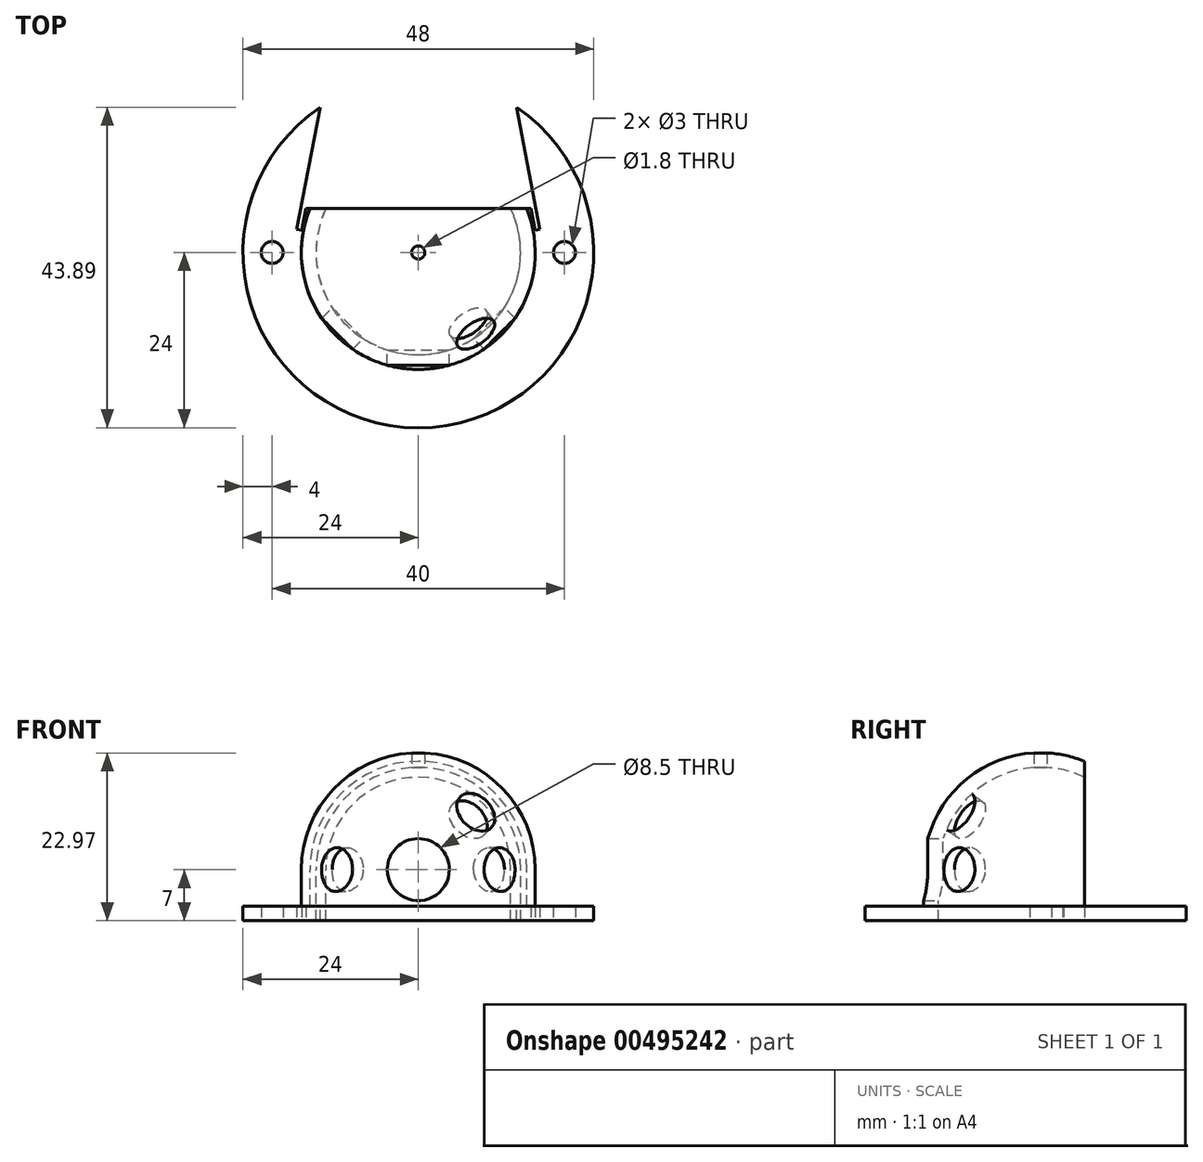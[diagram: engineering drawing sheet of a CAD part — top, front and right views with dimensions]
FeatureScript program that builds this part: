
annotation { "Feature Type Name" : "Feature", "Feature Type Description" : "" }
export const myFeature = defineFeature(function(context is Context, id is Id, definition is map)
    precondition{}
    {
        {
            var Q0;
            Q0=qCreatedBy(makeId("Front.planeOp"),FACE);
            var sketch = newSketch(context, id + "F0", { "sketchPlane" : qUnion([Q0])});
            skLineSegment(sketch, "E0", {"start": v(-14, -7) * mm, "end": v(-24, -7) * mm});
            skLineSegment(sketch, "E1", {"start": v(-24, -7) * mm, "end": v(-24, -5) * mm});
            skLineSegment(sketch, "E2", {"start": v(-24, -5) * mm, "end": v(-16, -5) * mm});
            skLineSegment(sketch, "E3", {"start": v(-16, -5) * mm, "end": v(-16, 0) * mm});
            skLineSegment(sketch, "E4", {"start": v(-14, -7) * mm, "end": v(-14, 0) * mm});
            skArc(sketch, "E5", {"start": v(0, 14) * mm, "mid": v(-9.9, 9.9) * mm, "end": v(-14, 0) * mm});
            skArc(sketch, "E6", {"start": v(0, 16) * mm, "mid": v(-11.31, 11.31) * mm, "end": v(-16, 0) * mm});
            skLineSegment(sketch, "E7", {"start": v(0, 16) * mm, "end": v(0, 14) * mm});
            skSolve(sketch);
        }
        {
            var Q0;
            Q0=qSketchRegion(id+"F0",true);
            var Q1;
            Q1=sQuery(id+"F0.wireOp",EDGE,"E7");
            revolve(context, id + "F1", {"entities" : qUnion([Q0]), "axis" : qUnion([Q1]), "revolveType" : RevolveType.FULL});
        }
        {
            var Q0;
            Q0=qCreatedBy(makeId("Front.planeOp"),FACE);
            var sketch = newSketch(context, id + "F2", { "sketchPlane" : qUnion([Q0])});
            skCircle(sketch, "E8", {"center": v(0, 0) * mm, "radius": 4.25 * mm});
            skSolve(sketch);
        }
        {
            var Q0;
            Q0=qSketchRegion(id+"F2",true);
            extrude(context, id + "F3", {"entities" : qUnion([Q0]), "operationType" : NewBodyOperationType.REMOVE, "depth" : 50 * mm});
        }
        {
            var Q0;
            Q0=qCreatedBy(makeId("Top.planeOp"),FACE);
            var sketch = newSketch(context, id + "F4", { "sketchPlane" : qUnion([Q0])});
            skLineSegment(sketch, "E9", {"start": v(-39.11, -39.11) * mm, "end": v(32.62, 32.62) * mm, "construction": true});
            skLineSegment(sketch, "E10", {"start": v(-37.35, 37.35) * mm, "end": v(42.98, -42.98) * mm, "construction": true});
            skSolve(sketch);
        }
        {
            var Q0;
            Q0=sQuery(id+"F4.wireOp",EDGE,"E10");
            cPlane(context, id + "F5", {"entities" : qUnion([Q0]), "cplaneType" : CPlaneType.LINE_ANGLE, "offset" : 25 * mm, "angle" : 90 * degree, "width" : 150 * mm, "height" : 150 * mm});
        }
        {
            var Q0;
            Q0=qCreatedBy(id+"F5.planeOp",FACE);
            var sketch = newSketch(context, id + "F6", { "sketchPlane" : qUnion([Q0])});
            skCircle(sketch, "E11", {"center": v(0, 0) * mm, "radius": 3 * mm});
            skSolve(sketch);
        }
        {
            var Q0;
            Q0=qSketchRegion(id+"F6",true);
            extrude(context, id + "F7", {"entities" : qUnion([Q0]), "operationType" : NewBodyOperationType.REMOVE, "oppositeDirection" : true, "depth" : 25 * mm});
        }
        {
            var Q0;
            Q0=qCreatedBy(makeId("Front.planeOp"),FACE);
            var sketch = newSketch(context, id + "F8", { "sketchPlane" : qUnion([Q0])});
            skLineSegment(sketch, "E12", {"start": v(0, 0) * mm, "end": v(30.29, 30.29) * mm, "construction": true});
            skLineSegment(sketch, "E13", {"start": v(0, 0) * mm, "end": v(-31.13, 31.13) * mm, "construction": true});
            skSolve(sketch);
        }
        {
            var Q0;
            Q0=sQuery(id+"F8.wireOp",EDGE,"E12");
            cPlane(context, id + "F9", {"entities" : qUnion([Q0]), "cplaneType" : CPlaneType.LINE_ANGLE, "offset" : 25 * mm, "angle" : 90 * degree, "width" : 150 * mm, "height" : 150 * mm});
        }
        {
            var Q0;
            Q0=qCreatedBy(id+"F9.planeOp",FACE);
            var sketch = newSketch(context, id + "F10", { "sketchPlane" : qUnion([Q0])});
            skLineSegment(sketch, "E14", {"start": v(0, 0) * mm, "end": v(19.81, 19.81) * mm, "construction": true});
            skLineSegment(sketch, "E15", {"start": v(16.68, 16.68) * mm, "end": v(14.56, 18.8) * mm});
            skLineSegment(sketch, "E16", {"start": v(14.56, 18.8) * mm, "end": v(1.88, 6.12) * mm});
            skLineSegment(sketch, "E17", {"start": v(1.88, 6.12) * mm, "end": v(4, 4) * mm});
            skLineSegment(sketch, "E18", {"start": v(4, 4) * mm, "end": v(16.68, 16.68) * mm});
            skSolve(sketch);
        }
        {
            var Q0;
            Q0=qSketchRegion(id+"F10",true);
            var Q1;
            Q1=sQuery(id+"F10.wireOp",EDGE,"E18");
            revolve(context, id + "F11", {"operationType" : NewBodyOperationType.REMOVE, "entities" : qUnion([Q0]), "axis" : qUnion([Q1]), "revolveType" : RevolveType.FULL, "oppositeDirection" : true});
        }
        {
            var Q0;
            Q0=sQuery(id+"F4.wireOp",EDGE,"E9");
            cPlane(context, id + "F12", {"entities" : qUnion([Q0]), "cplaneType" : CPlaneType.LINE_ANGLE, "offset" : 25 * mm, "angle" : 90 * degree, "width" : 150 * mm, "height" : 150 * mm});
        }
        {
            var Q0;
            Q0=qCreatedBy(id+"F12.planeOp",FACE);
            var sketch = newSketch(context, id + "F13", { "sketchPlane" : qUnion([Q0])});
            skCircle(sketch, "E19", {"center": v(0, 0) * mm, "radius": 3 * mm});
            skSolve(sketch);
        }
        {
            var Q0;
            Q0=qSketchRegion(id+"F13",true);
            extrude(context, id + "F14", {"entities" : qUnion([Q0]), "operationType" : NewBodyOperationType.REMOVE, "depth" : 25 * mm});
        }
        {
            var Q0;
            Q0=sQuery(id+"F8.wireOp",EDGE,"E13");
            cPlane(context, id + "F15", {"entities" : qUnion([Q0]), "cplaneType" : CPlaneType.LINE_ANGLE, "offset" : 25 * mm, "angle" : 90 * degree, "width" : 150 * mm, "height" : 150 * mm});
        }
        {
            var Q0;
            Q0=qCreatedBy(id+"F15.planeOp",FACE);
            var sketch = newSketch(context, id + "F16", { "sketchPlane" : qUnion([Q0])});
            skLineSegment(sketch, "E20", {"start": v(0, 0) * mm, "end": v(-61.78, -61.78) * mm});
            skSolve(sketch);
        }
        {
            var Q0;
            Q0=qCreatedBy(makeId("Top.planeOp"),FACE);
            var sketch = newSketch(context, id + "F17", { "sketchPlane" : qUnion([Q0])});
            skCircle(sketch, "E21", {"center": v(0, 0) * mm, "radius": 0.9 * mm});
            skSolve(sketch);
        }
        {
            var Q0;
            Q0=qSketchRegion(id+"F17",true);
            extrude(context, id + "F18", {"entities" : qUnion([Q0]), "operationType" : NewBodyOperationType.REMOVE, "depth" : 30.1 * mm});
        }
        {
            var Q0;
            Q0=qCreatedBy(makeId("Right.planeOp"),FACE);
            var sketch = newSketch(context, id + "F19", { "sketchPlane" : qUnion([Q0])});
            skLineSegment(sketch, "E22", {"start": v(-34.54, 0) * mm, "end": v(39.7, 0) * mm, "construction": true});
            skSolve(sketch);
        }
        {
            var Q0;
            Q0=qCreatedBy(makeId("Top.planeOp"),FACE);
            var sketch = newSketch(context, id + "F20", { "sketchPlane" : qUnion([Q0])});
            skLineSegment(sketch, "E23", {"start": v(0, 0) * mm, "end": v(0, -71.29) * mm, "construction": true});
            skSolve(sketch);
        }
        {
            var Q0;
            Q0=makeQuery(id+"F1.opRevolve","SWEPT_FACE",FACE,{"disambiguationData":[OSD([sQuery(id+"F0.wireOp",EDGE,"E0")])]});
            cPlane(context, id + "F21", {"entities" : qUnion([Q0]), "cplaneType" : CPlaneType.OFFSET, "offset" : 7 * mm, "width" : 150 * mm, "height" : 150 * mm});
        }
        {
            var Q0;
            Q0=qCreatedBy(id+"F21.planeOp",FACE);
            var sketch = newSketch(context, id + "F22", { "sketchPlane" : qUnion([Q0])});
            skPoint(sketch, "E24", {"position": v(-15.4, -6) * mm});
            skSolve(sketch);
        }
        {
            var Q0;
            Q0=qCreatedBy(id+"F21.planeOp",FACE);
            var sketch = newSketch(context, id + "F23", { "sketchPlane" : qUnion([Q0])});
            skLineSegment(sketch, "E25", {"start": v(-15.4, -6) * mm, "end": v(15.4, -6) * mm});
            skLineSegment(sketch, "E26", {"start": v(15.4, -6) * mm, "end": v(15.96, -3.05) * mm});
            skLineSegment(sketch, "E27", {"start": v(15.96, -3.05) * mm, "end": v(16.64, -3.19) * mm});
            skLineSegment(sketch, "E28", {"start": v(16.64, -3.19) * mm, "end": v(12.49, -24.8) * mm});
            skLineSegment(sketch, "E29", {"start": v(12.49, -24.8) * mm, "end": v(-12.49, -24.8) * mm});
            skLineSegment(sketch, "E30", {"start": v(-12.49, -24.8) * mm, "end": v(-16.64, -3.19) * mm});
            skLineSegment(sketch, "E31", {"start": v(-16.64, -3.19) * mm, "end": v(-15.96, -3.05) * mm});
            skLineSegment(sketch, "E32", {"start": v(-15.96, -3.05) * mm, "end": v(-15.39, -6) * mm});
            skSolve(sketch);
        }
        {
            var Q0;
            Q0 = qSketchRegion(id + "F23", true);
            extrude(context, id + "F24", {"entities" : qUnion([Q0]), "operationType" : NewBodyOperationType.REMOVE, "endBound" : BoundingType.THROUGH_ALL, "oppositeDirection" : true, "depth" : 25 * mm});
        }
        {
            var Q0;
            Q0=qCreatedBy(id+"F21.planeOp",FACE);
            var sketch = newSketch(context, id + "F25", { "sketchPlane" : qUnion([Q0])});
            skLineSegment(sketch, "E33", {"start": v(-27.44, 0) * mm, "end": v(34.18, 0) * mm, "construction": true});
            skCircle(sketch, "E34", {"center": v(0, 0) * mm, "radius": 20 * mm, "construction": true});
            skCircle(sketch, "E35", {"center": v(-20, 0) * mm, "radius": 1.5 * mm});
            skCircle(sketch, "E36", {"center": v(20, 0) * mm, "radius": 1.5 * mm});
            skSolve(sketch);
        }
        {
            var Q0;
            Q0 = qSketchRegion(id + "F25", true);
            extrude(context, id + "F26", {"entities" : qUnion([Q0]), "operationType" : NewBodyOperationType.REMOVE, "endBound" : BoundingType.THROUGH_ALL, "oppositeDirection" : true, "depth" : 25 * mm});
        }
    });
